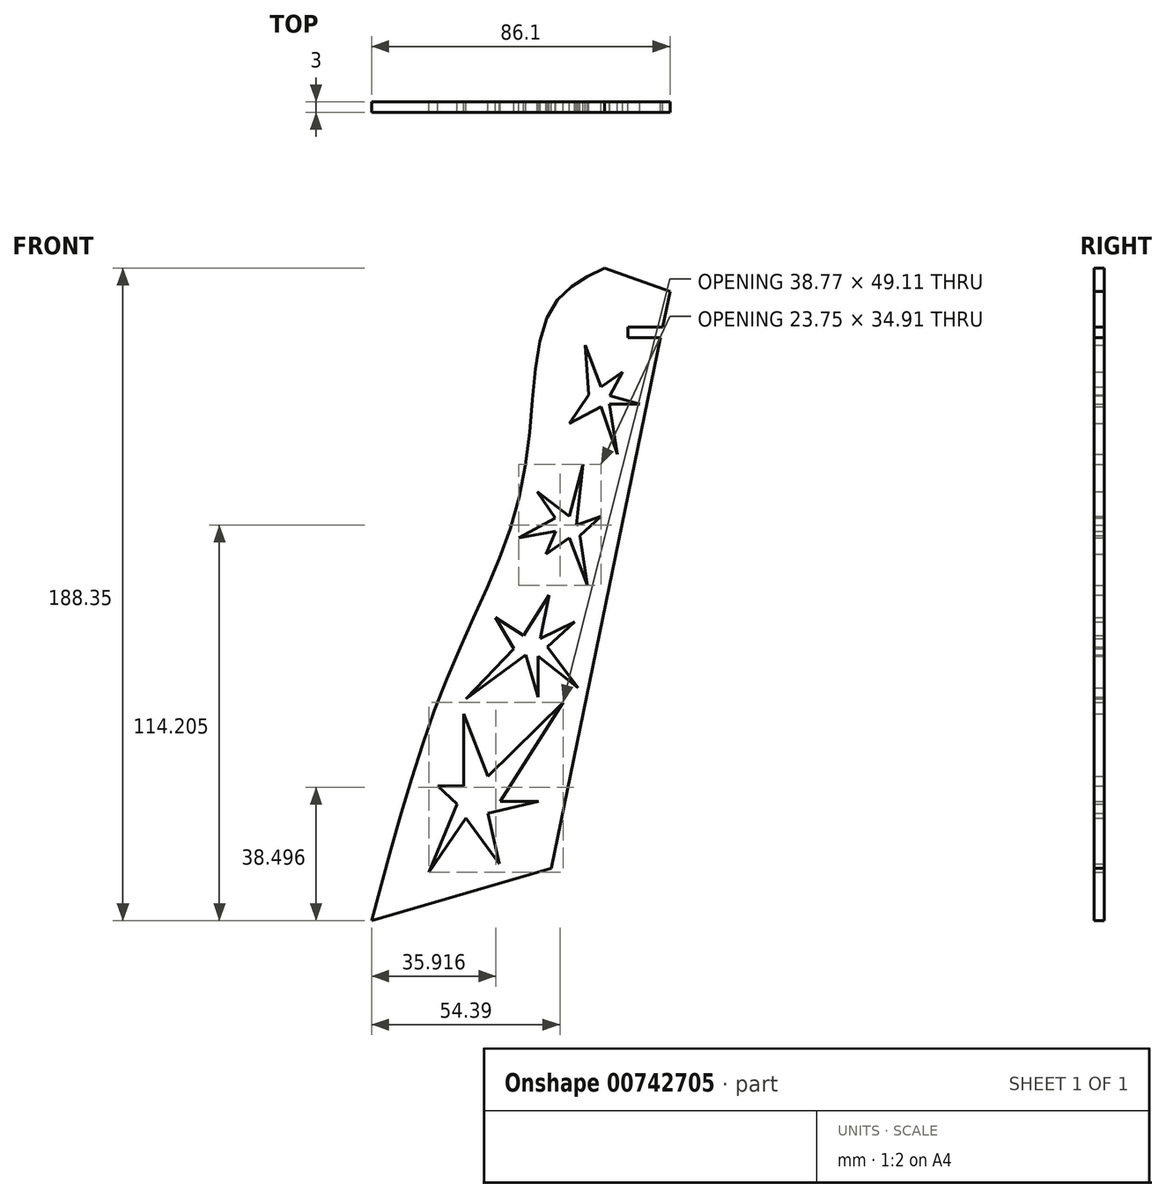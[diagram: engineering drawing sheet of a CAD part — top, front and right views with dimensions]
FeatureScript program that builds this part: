
annotation { "Feature Type Name" : "Feature", "Feature Type Description" : "" }
export const myFeature = defineFeature(function(context is Context, id is Id, definition is map)
    precondition{}
    {
        {
            var Q0;
            Q0=qCreatedBy(makeId("Front.planeOp"),FACE);
            var sketch = newSketch(context, id + "F0", { "sketchPlane" : qUnion([Q0])});
            skLineSegment(sketch, "E0", {"start": v(-69.42, 162.61) * mm, "end": v(-50.59, 155.89) * mm});
            skLineSegment(sketch, "E1", {"start": v(-50.59, 155.89) * mm, "end": v(-84.87, -10.62) * mm});
            skLineSegment(sketch, "E2", {"start": v(-84.87, -10.62) * mm, "end": v(-136.69, -25.74) * mm});
            skLineSegment(sketch, "E3", {"start": v(-110.14, 13.08) * mm, "end": v(-110.14, 34.02) * mm});
            skLineSegment(sketch, "E4", {"start": v(-110.14, 34.02) * mm, "end": v(-103.15, 15.96) * mm});
            skLineSegment(sketch, "E5", {"start": v(-103.15, 15.96) * mm, "end": v(-81.39, 37.3) * mm});
            skLineSegment(sketch, "E6", {"start": v(-81.39, 37.3) * mm, "end": v(-99.56, 8.67) * mm});
            skLineSegment(sketch, "E7", {"start": v(-99.56, 8.67) * mm, "end": v(-88.48, 8.67) * mm});
            skLineSegment(sketch, "E8", {"start": v(-88.48, 8.67) * mm, "end": v(-103.15, 5.28) * mm});
            skLineSegment(sketch, "E9", {"start": v(-103.15, 5.28) * mm, "end": v(-99.77, -9.36) * mm});
            skLineSegment(sketch, "E10", {"start": v(-99.77, -9.36) * mm, "end": v(-109.48, 3.8) * mm});
            skLineSegment(sketch, "E11", {"start": v(-109.48, 3.8) * mm, "end": v(-120.16, -11.8) * mm});
            skLineSegment(sketch, "E12", {"start": v(-120.16, -11.8) * mm, "end": v(-111.95, 7.91) * mm});
            skLineSegment(sketch, "E13", {"start": v(-110.14, 13.08) * mm, "end": v(-117.53, 13.08) * mm});
            skLineSegment(sketch, "E14", {"start": v(-117.53, 13.08) * mm, "end": v(-111.95, 7.91) * mm});
            skLineSegment(sketch, "E15", {"start": v(-95.56, 52.7) * mm, "end": v(-100.95, 61.74) * mm});
            skLineSegment(sketch, "E16", {"start": v(-100.95, 61.74) * mm, "end": v(-92.8, 56.57) * mm});
            skLineSegment(sketch, "E17", {"start": v(-92.8, 56.57) * mm, "end": v(-85.43, 68.2) * mm});
            skLineSegment(sketch, "E18", {"start": v(-85.43, 68.2) * mm, "end": v(-88, 55.67) * mm});
            skLineSegment(sketch, "E19", {"start": v(-88, 55.67) * mm, "end": v(-78.1, 60.51) * mm});
            skLineSegment(sketch, "E20", {"start": v(-78.1, 60.51) * mm, "end": v(-85.9, 53.33) * mm});
            skLineSegment(sketch, "E21", {"start": v(-85.9, 53.33) * mm, "end": v(-77.08, 41.42) * mm});
            skLineSegment(sketch, "E22", {"start": v(-77.08, 41.42) * mm, "end": v(-88.58, 50.66) * mm});
            skLineSegment(sketch, "E23", {"start": v(-88.58, 50.66) * mm, "end": v(-88.58, 38.75) * mm});
            skLineSegment(sketch, "E24", {"start": v(-88.58, 38.75) * mm, "end": v(-92.13, 50.93) * mm});
            skLineSegment(sketch, "E25", {"start": v(-92.13, 50.93) * mm, "end": v(-109.48, 38.34) * mm});
            skLineSegment(sketch, "E26", {"start": v(-109.48, 38.34) * mm, "end": v(-95.56, 52.7) * mm});
            skLineSegment(sketch, "E27", {"start": v(-83.7, 90.52) * mm, "end": v(-88.84, 98.12) * mm});
            skLineSegment(sketch, "E28", {"start": v(-88.84, 98.12) * mm, "end": v(-79.63, 90.93) * mm});
            skLineSegment(sketch, "E29", {"start": v(-79.63, 90.93) * mm, "end": v(-75.7, 105.92) * mm});
            skLineSegment(sketch, "E30", {"start": v(-75.7, 105.92) * mm, "end": v(-77.54, 88.47) * mm});
            skLineSegment(sketch, "E31", {"start": v(-77.54, 88.47) * mm, "end": v(-70.42, 90.93) * mm});
            skLineSegment(sketch, "E32", {"start": v(-70.42, 90.93) * mm, "end": v(-76.52, 85.39) * mm});
            skLineSegment(sketch, "E33", {"start": v(-76.52, 85.39) * mm, "end": v(-74.46, 71.01) * mm});
            skLineSegment(sketch, "E34", {"start": v(-74.46, 71.01) * mm, "end": v(-79.63, 84.77) * mm});
            skLineSegment(sketch, "E35", {"start": v(-79.63, 84.77) * mm, "end": v(-86.37, 80.05) * mm});
            skLineSegment(sketch, "E36", {"start": v(-86.37, 80.05) * mm, "end": v(-83.5, 86.62) * mm});
            skLineSegment(sketch, "E37", {"start": v(-83.5, 86.62) * mm, "end": v(-94.18, 84.77) * mm});
            skLineSegment(sketch, "E38", {"start": v(-94.18, 84.77) * mm, "end": v(-83.7, 90.52) * mm});
            skLineSegment(sketch, "E39", {"start": v(-70.42, 128.37) * mm, "end": v(-64.27, 132.69) * mm});
            skLineSegment(sketch, "E40", {"start": v(-64.27, 132.69) * mm, "end": v(-67.9, 125.78) * mm});
            skLineSegment(sketch, "E41", {"start": v(-67.9, 125.78) * mm, "end": v(-59.26, 123.36) * mm});
            skLineSegment(sketch, "E42", {"start": v(-59.26, 123.36) * mm, "end": v(-68.07, 123.36) * mm});
            skLineSegment(sketch, "E43", {"start": v(-68.07, 123.36) * mm, "end": v(-65.82, 108.86) * mm});
            skLineSegment(sketch, "E44", {"start": v(-65.82, 108.86) * mm, "end": v(-70.42, 122.67) * mm});
            skLineSegment(sketch, "E45", {"start": v(-70.42, 122.67) * mm, "end": v(-79.63, 117.78) * mm});
            skLineSegment(sketch, "E46", {"start": v(-79.63, 117.78) * mm, "end": v(-74.02, 126.06) * mm});
            skLineSegment(sketch, "E47", {"start": v(-75, 140.4) * mm, "end": v(-70.42, 128.37) * mm});
            skLineSegment(sketch, "E48", {"start": v(-75, 140.4) * mm, "end": v(-74.02, 126.06) * mm});
            skFitSpline(sketch, "E49", {"points": [v(-69.42, 162.61) * mm, v(-85.32, 149.93) * mm, v(-93.13, 100.6) * mm, v(-114.62, 44.93) * mm, v(-136.69, -25.74) * mm], "startDerivative": vector(-115.22, -53.9) * mm, "endDerivative": vector(-64.5, -239.44) * mm});
            skSolve(sketch);
        }
        {
            var Q0;
            Q0 = qSketchRegion(id + "F0", true);
            extrude(context, id + "F1", {"entities" : qUnion([Q0]), "depth" : 3 * mm, "offsetDistance" : 25 * mm});
        }
        {
            var Q0;
            Q0=qCreatedBy(makeId("Front.planeOp"),FACE);
            var sketch = newSketch(context, id + "F2", { "sketchPlane" : qUnion([Q0])});
            skLineSegment(sketch, "E50.bottom", {"start": v(-42.66, 142.56) * mm, "end": v(-62.66, 142.56) * mm});
            skLineSegment(sketch, "E50.top", {"start": v(-42.66, 145.56) * mm, "end": v(-62.66, 145.56) * mm});
            skLineSegment(sketch, "E50.left", {"start": v(-42.66, 142.56) * mm, "end": v(-42.66, 145.56) * mm});
            skLineSegment(sketch, "E50.right", {"start": v(-62.66, 142.56) * mm, "end": v(-62.66, 145.56) * mm});
            skPoint(sketch, "E50.middle", {"position": v(-52.66, 144.06) * mm});
            skSolve(sketch);
        }
        {
            var Q0;
            Q0 = qSketchRegion(id + "F2", true);
            extrude(context, id + "F3", {"entities" : qUnion([Q0]), "operationType" : NewBodyOperationType.REMOVE, "depth" : 25 * mm, "offsetDistance" : 25 * mm});
        }
    });
